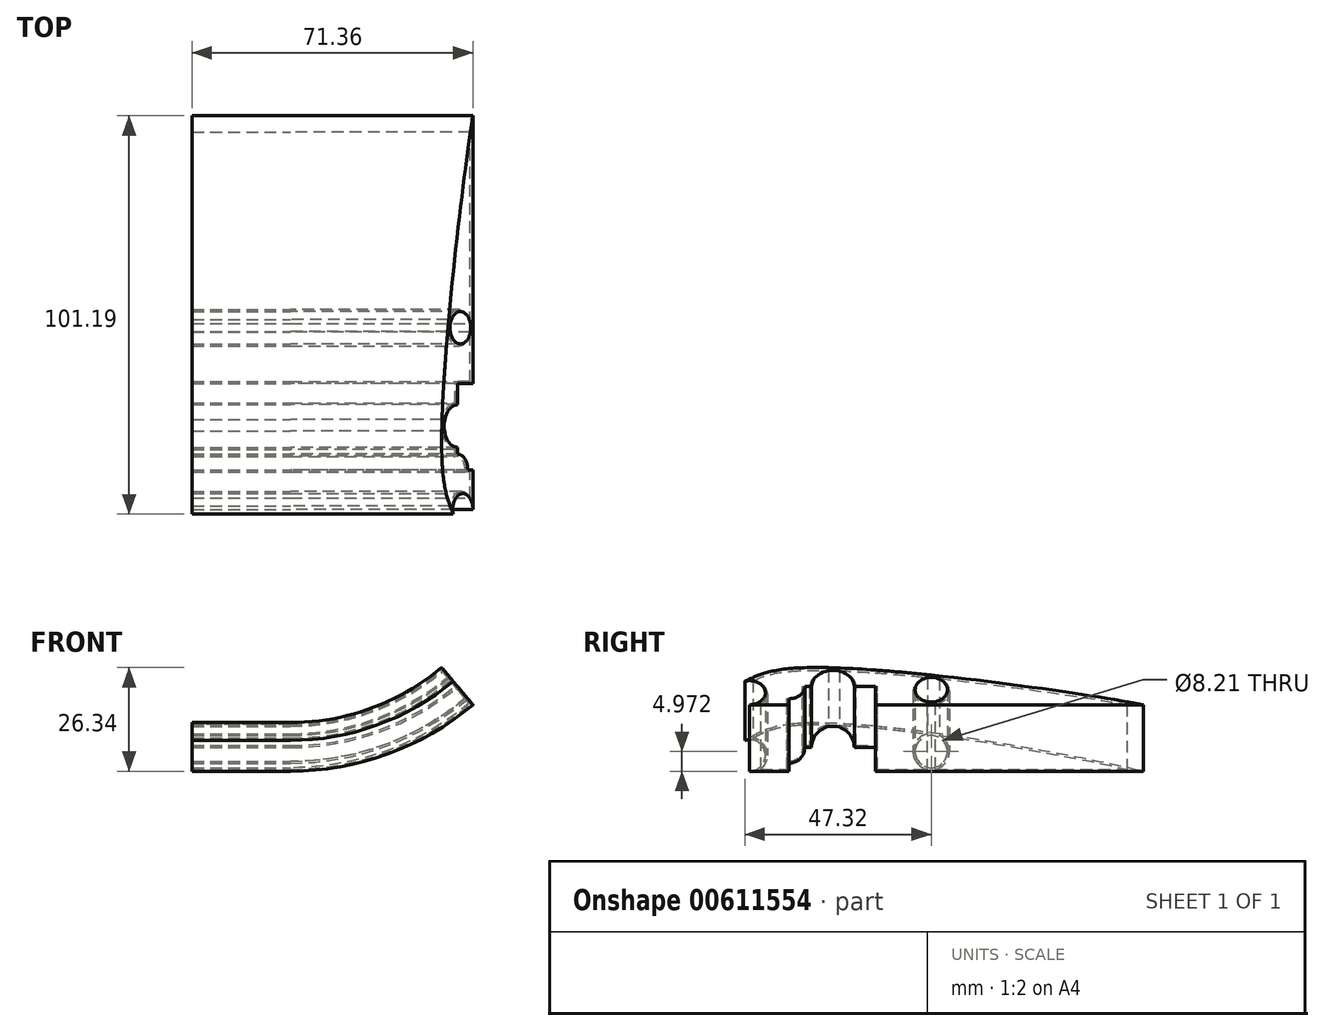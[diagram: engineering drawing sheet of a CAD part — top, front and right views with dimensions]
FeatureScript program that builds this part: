
annotation { "Feature Type Name" : "Feature", "Feature Type Description" : "" }
export const myFeature = defineFeature(function(context is Context, id is Id, definition is map)
    precondition{}
    {
        {
            var Q0;
            Q0=qCreatedBy(makeId("Right.planeOp"),FACE);
            var sketch = newSketch(context, id + "F0", { "sketchPlane" : qUnion([Q0])});
            skLineSegment(sketch, "E0", {"start": v(-18.28, -12.55) * mm, "end": v(-8.28, -12.55) * mm});
            skLineSegment(sketch, "E1", {"start": v(-8.28, -12.55) * mm, "end": v(17.32, -12.55) * mm});
            skLineSegment(sketch, "E2", {"start": v(-18.28, -12.55) * mm, "end": v(-18.28, -4.55) * mm});
            skLineSegment(sketch, "E3", {"start": v(-8.28, -12.55) * mm, "end": v(-8.28, -0.55) * mm});
            skLineSegment(sketch, "E4", {"start": v(-18.28, -12.55) * mm, "end": v(-18.28, -8.55) * mm});
            skArc(sketch, "E5", {"start": v(-18.28, -12.55) * mm, "mid": v(-22.14, -9.6) * mm, "end": v(-20.3, -5.1) * mm});
            skFitSpline(sketch, "E6", {"points": [v(-20.3, -5.1) * mm, v(-8.28, -0.55) * mm, v(81.72, -12.55) * mm], "startDerivative": vector(25.72, 9) * mm, "endDerivative": vector(55.93, -14.48) * mm});
            skLineSegment(sketch, "E7", {"start": v(17.32, -12.55) * mm, "end": v(81.72, -12.55) * mm});
            skLineSegment(sketch, "E8", {"start": v(17.32, -12.55) * mm, "end": v(13.65, -12.55) * mm});
            skLineSegment(sketch, "E9", {"start": v(13.65, -12.55) * mm, "end": v(13.65, -1.03) * mm});
            skCircle(sketch, "E10", {"center": v(-18.28, -8.55) * mm, "radius": 4 * mm});
            skLineSegment(sketch, "E11", {"start": v(-8.28, -12.55) * mm, "end": v(-8.28, -6.55) * mm});
            skCircle(sketch, "E12", {"center": v(-8.28, -6.55) * mm, "radius": 4 * mm});
            skLineSegment(sketch, "E13.right", {"start": v(27.85, 2.27) * mm, "end": v(27.85, -14.67) * mm});
            skLineSegment(sketch, "E14", {"start": v(-8.28, -6.55) * mm, "end": v(2.87, -6.55) * mm});
            skLineSegment(sketch, "E15", {"start": v(2.87, -6.55) * mm, "end": v(13.65, -6.55) * mm});
            skLineSegment(sketch, "E16", {"start": v(13.65, -6.55) * mm, "end": v(27.85, -7.58) * mm});
            skCircle(sketch, "E17", {"center": v(2.87, -6.55) * mm, "radius": 5.42 * mm});
            skCircle(sketch, "E18", {"center": v(27.85, -7.58) * mm, "radius": 4.1 * mm});
            skLineSegment(sketch, "E19", {"start": v(-18.28, -8.55) * mm, "end": v(-18.28, 8.18) * mm});
            skLineSegment(sketch, "E20", {"start": v(-18.28, 8.18) * mm, "end": v(13.32, 8.18) * mm});
            skLineSegment(sketch, "E21", {"start": v(-18.28, 8.18) * mm, "end": v(-18.28, 22.4) * mm});
            skLineSegment(sketch, "E22", {"start": v(-18.28, 22.4) * mm, "end": v(16.16, 22.4) * mm});
            skLineSegment(sketch, "E23", {"start": v(-18.28, 22.4) * mm, "end": v(-18.28, 59.58) * mm});
            skPoint(sketch, "E23.endSnap0", {"position": v(-18.28, 15.29) * mm});
            skLineSegment(sketch, "E24", {"start": v(-18.28, 59.58) * mm, "end": v(2.68, 59.58) * mm});
            skSolve(sketch);
        }
        {
            var Q0;
            {var subQ1=sQuery(id+"F0.wireOp",EDGE,"E7");var subQ5=sQuery(id+"F0.wireOp",EDGE,"E6");var subQ6=makeQuery(id+"F0.imprint","INTERSECT",VERTEX,{"derivedFrom":[subQ5,subQ1]});Q0=makeQuery(id+"F0.imprint","IMPRINT",FACE,{"disambiguationData":[TD([[makeQuery(id+"F0.imprint","IMPRINT",EDGE,{"disambiguationData":[TD([[subQ6,1.0]])],"derivedFrom":subQ5}),-1.0]])]});}
            var Q1;
            {var subQ1=sQuery(id+"F0.wireOp",EDGE,"E8");Q1=makeQuery(id+"F0.imprint","IMPRINT",FACE,{"disambiguationData":[TD([[makeQuery(id+"F0.imprint","IMPRINT",EDGE,{"derivedFrom":subQ1}),-1.0]])]});}
            var Q2;
            {var subQ1=sQuery(id+"F0.wireOp",EDGE,"E6");var subQ5=sQuery(id+"F0.wireOp",EDGE,"E9");var subQ6=makeQuery(id+"F0.imprint","INTERSECT",VERTEX,{"derivedFrom":[subQ1,subQ5]});Q2=makeQuery(id+"F0.imprint","IMPRINT",FACE,{"disambiguationData":[TD([[makeQuery(id+"F0.imprint","IMPRINT",EDGE,{"disambiguationData":[TD([[subQ6,-1.0]])],"derivedFrom":subQ1}),-1.0]])]});}
            var Q3;
            {var subQ1=sQuery(id+"F0.wireOp",EDGE,"E3");var subQ10=sQuery(id+"F0.wireOp",EDGE,"E6");var subQ12=makeQuery(id+"F0.imprint","INTERSECT",VERTEX,{"derivedFrom":[subQ1,subQ10]});Q3=makeQuery(id+"F0.imprint","IMPRINT",FACE,{"disambiguationData":[TD([[makeQuery(id+"F0.imprint","IMPRINT",EDGE,{"disambiguationData":[TD([[subQ12,1.0]])],"derivedFrom":subQ1}),-1.0]])]});}
            var Q4;
            {var subQ1=sQuery(id+"F0.wireOp",EDGE,"E1");Q4=makeQuery(id+"F0.imprint","IMPRINT",FACE,{"disambiguationData":[TD([[makeQuery(id+"F0.imprint","IMPRINT",EDGE,{"derivedFrom":subQ1}),1.0]])]});}
            var Q5;
            {var subQ1=sQuery(id+"F0.wireOp",EDGE,"E0");Q5=makeQuery(id+"F0.imprint","IMPRINT",FACE,{"disambiguationData":[TD([[makeQuery(id+"F0.imprint","IMPRINT",EDGE,{"derivedFrom":subQ1}),1.0]])]});}
            var Q6;
            {var subQ0=sQuery(id+"F0.wireOp",EDGE,"E4");Q6=makeQuery(id+"F0.imprint","IMPRINT",FACE,{"disambiguationData":[TD([[makeQuery(id+"F0.imprint","IMPRINT",EDGE,{"derivedFrom":subQ0}),-1.0]])]});}
            var Q7;
            {var subQ1=sQuery(id+"F0.wireOp",EDGE,"E4");Q7=makeQuery(id+"F0.imprint","IMPRINT",FACE,{"disambiguationData":[TD([[makeQuery(id+"F0.imprint","IMPRINT",EDGE,{"derivedFrom":subQ1}),1.0]])]});}
            var Q8;
            {var subQ0=sQuery(id+"F0.wireOp",EDGE,"E19");var subQ1=sQuery(id+"F0.wireOp",EDGE,"E6");var subQ2=makeQuery(id+"F0.imprint","INTERSECT",VERTEX,{"derivedFrom":[subQ1,subQ0]});Q8=makeQuery(id+"F0.imprint","IMPRINT",FACE,{"disambiguationData":[TD([[makeQuery(id+"F0.imprint","IMPRINT",EDGE,{"disambiguationData":[TD([[subQ2,1.0]])],"derivedFrom":subQ1}),-1.0]])]});}
            var Q9;
            {var subQ1=sQuery(id+"F0.wireOp",EDGE,"E3");var subQ3=sQuery(id+"F0.wireOp",EDGE,"E12");var subQ4=makeQuery(id+"F0.imprint","INTERSECT",VERTEX,{"derivedFrom":[subQ1,subQ3]});Q9=makeQuery(id+"F0.imprint","IMPRINT",FACE,{"disambiguationData":[TD([[makeQuery(id+"F0.imprint","IMPRINT",EDGE,{"disambiguationData":[TD([[subQ4,-1.0]])],"derivedFrom":subQ3}),1.0]])]});}
            var Q10;
            {var subQ1=sQuery(id+"F0.wireOp",EDGE,"E11");var subQ3=sQuery(id+"F0.wireOp",EDGE,"E12");var subQ4=makeQuery(id+"F0.imprint","INTERSECT",VERTEX,{"derivedFrom":[subQ1,subQ3]});Q10=makeQuery(id+"F0.imprint","IMPRINT",FACE,{"disambiguationData":[TD([[makeQuery(id+"F0.imprint","IMPRINT",EDGE,{"disambiguationData":[TD([[subQ4,-1.0]])],"derivedFrom":subQ3}),1.0]])]});}
            var Q11;
            {var subQ1=sQuery(id+"F0.wireOp",EDGE,"E3");var subQ3=sQuery(id+"F0.wireOp",EDGE,"E12");var subQ4=makeQuery(id+"F0.imprint","INTERSECT",VERTEX,{"derivedFrom":[subQ1,subQ3]});Q11=makeQuery(id+"F0.imprint","IMPRINT",FACE,{"disambiguationData":[TD([[makeQuery(id+"F0.imprint","IMPRINT",EDGE,{"disambiguationData":[TD([[subQ4,1.0]])],"derivedFrom":subQ3}),1.0]])]});}
            var Q12;
            Q12=sQuery(id+"F0.wireOp",EDGE,"E24");
            revolve(context, id + "F1", {"entities" : qUnion([Q0, Q1, Q2, Q3, Q4, Q5, Q6, Q7, Q8, Q9, Q10, Q11]), "axis" : qUnion([Q12]), "revolveType" : RevolveType.ONE_DIRECTION, "oppositeDirection" : true, "angle" : 40 * degree});
        }
        {
            var Q0;
            Q0=makeQuery(id+"F1.opRevolve","CAP_FACE",FACE,{"disambiguationData":[OSD([sQuery(id+"F0.wireOp",EDGE,"E0"),sQuery(id+"F0.wireOp",EDGE,"E1"),sQuery(id+"F0.wireOp",EDGE,"E6"),sQuery(id+"F0.wireOp",EDGE,"E7"),sQuery(id+"F0.wireOp",EDGE,"E8"),sQuery(id+"F0.wireOp",EDGE,"E10"),sQuery(id+"F0.wireOp",EDGE,"E12"),sQuery(id+"F0.wireOp",EDGE,"E17"),sQuery(id+"F0.wireOp",EDGE,"E18")])],"isStart":true});
            extrude(context, id + "F2", {"entities" : qUnion([Q0]), "operationType" : NewBodyOperationType.ADD, "depth" : 25 * mm, "offsetDistance" : 25 * mm});
        }
        {
            var Q0;
            Q0=makeQuery(id+"F2.opExtrude","CAP_FACE",FACE,{"disambiguationData":[OSD([sQuery(id+"F0.wireOp",EDGE,"E0"),sQuery(id+"F0.wireOp",EDGE,"E1"),sQuery(id+"F0.wireOp",EDGE,"E6"),sQuery(id+"F0.wireOp",EDGE,"E7"),sQuery(id+"F0.wireOp",EDGE,"E8"),sQuery(id+"F0.wireOp",EDGE,"E10"),sQuery(id+"F0.wireOp",EDGE,"E17"),sQuery(id+"F0.wireOp",EDGE,"E18")])],"isStart":false});
            shell(context, id + "F3", {"entities" : qUnion([Q0]), "thickness" : 0.5 * mm});
        }
    });
